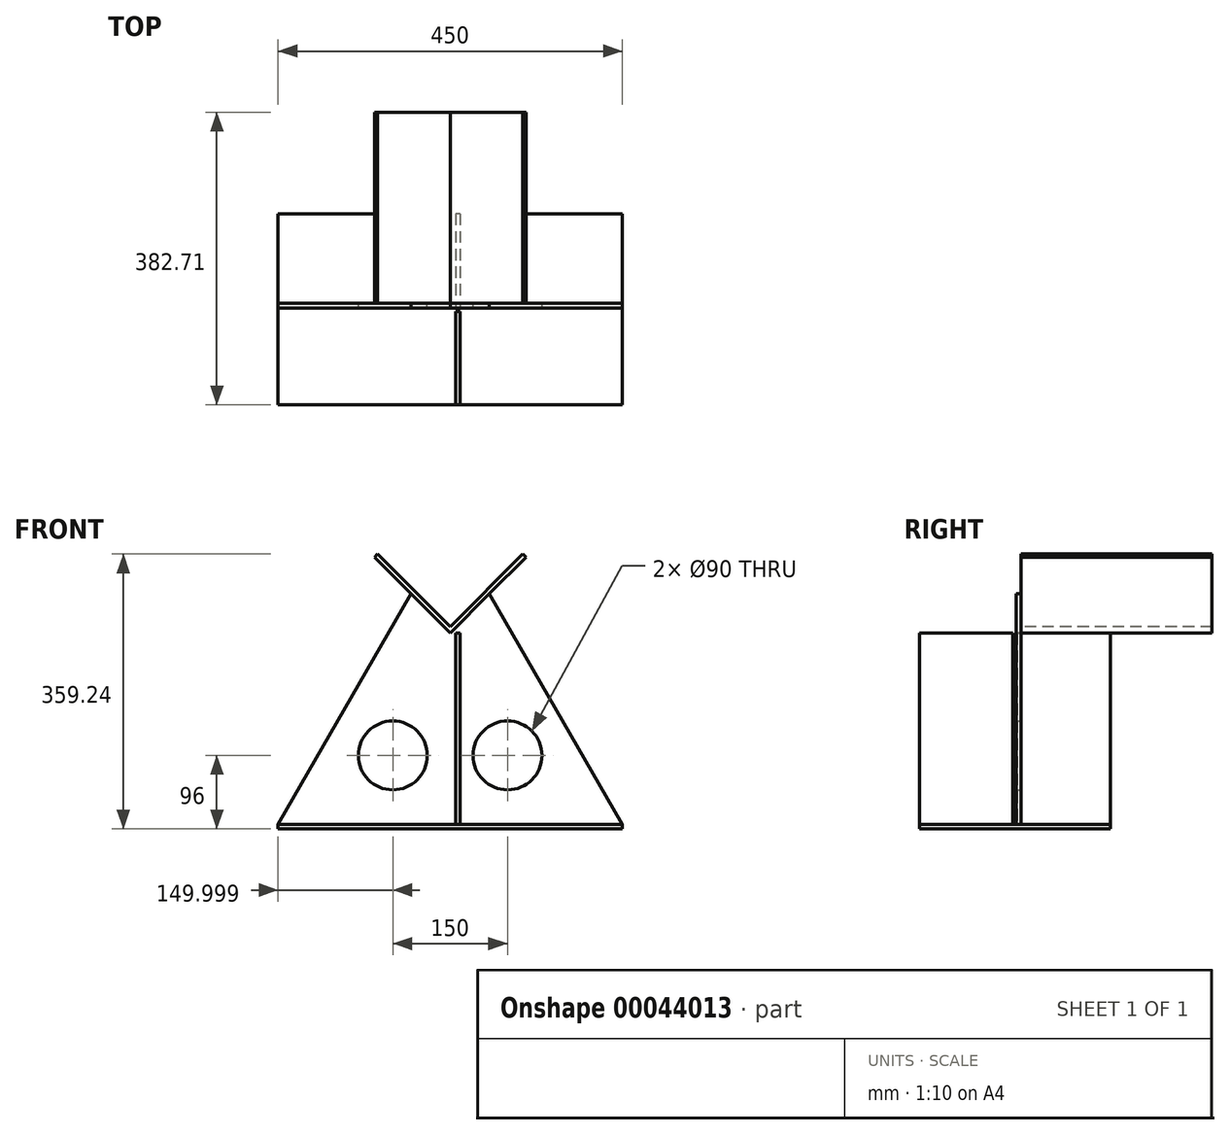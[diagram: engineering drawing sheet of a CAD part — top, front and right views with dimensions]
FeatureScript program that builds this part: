
annotation { "Feature Type Name" : "Feature", "Feature Type Description" : "" }
export const myFeature = defineFeature(function(context is Context, id is Id, definition is map)
    precondition{}
    {
        {
            var Q0;
            Q0=qCreatedBy(makeId("Top.planeOp"),FACE);
            var sketch = newSketch(context, id + "F0", { "sketchPlane" : qUnion([Q0])});
            skLineSegment(sketch, "E0.bottom", {"start": v(-231.25, -129.7) * mm, "end": v(218.75, -129.7) * mm});
            skLineSegment(sketch, "E0.top", {"start": v(-231.25, 120.3) * mm, "end": v(218.75, 120.3) * mm});
            skLineSegment(sketch, "E0.left", {"start": v(-231.25, -129.7) * mm, "end": v(-231.25, 120.3) * mm});
            skLineSegment(sketch, "E0.right", {"start": v(218.75, -129.7) * mm, "end": v(218.75, 120.3) * mm});
            skSolve(sketch);
        }
        {
            var Q0;
            Q0=qSketchRegion(id+"F0",true);
            var Q1;
            Q1=makeQuery(id+"F0.imprint","IMPRINT",FACE,{"disambiguationData":[TD([[makeQuery(id+"F0.imprint","IMPRINT",EDGE,{"derivedFrom":sQuery(id+"F0.wireOp",EDGE,"E0.bottom")}),1.0]])]});
            extrude(context, id + "F1", {"entities" : qUnion([Q0, Q1]), "depth" : 6 * mm});
        }
        {
            var Q0;
            Q0=qCreatedBy(makeId("Front.planeOp"),FACE);
            var sketch = newSketch(context, id + "F2", { "sketchPlane" : qUnion([Q0])});
            skLineSegment(sketch, "E1", {"start": v(-231.25, 6) * mm, "end": v(-57.39, 307.14) * mm});
            skLineSegment(sketch, "E2", {"start": v(218.75, 6) * mm, "end": v(44.89, 307.14) * mm});
            skLineSegment(sketch, "E3", {"start": v(-6.25, 256) * mm, "end": v(-57.39, 307.14) * mm});
            skLineSegment(sketch, "E4", {"start": v(-6.25, 256) * mm, "end": v(44.89, 307.14) * mm});
            skPoint(sketch, "E5.0", {"position": v(0, 0) * mm});
            skLineSegment(sketch, "E6", {"start": v(218.75, 6) * mm, "end": v(-231.25, 6) * mm});
            skCircle(sketch, "E7", {"center": v(-81.25, 96) * mm, "radius": 45 * mm});
            skCircle(sketch, "E8", {"center": v(68.75, 96) * mm, "radius": 45 * mm});
            skSolve(sketch);
        }
        {
            var Q0;
            Q0=makeQuery(id+"F2.imprint","IMPRINT",FACE,{"disambiguationData":[TD([[makeQuery(id+"F2.imprint","IMPRINT",EDGE,{"derivedFrom":sQuery(id+"F2.wireOp",EDGE,"E1")}),-1.0]])]});
            extrude(context, id + "F3", {"entities" : qUnion([Q0]), "depth" : 3 * mm, "hasSecondDirection" : true, "secondDirectionOppositeDirection" : true, "secondDirectionDepth" : 3 * mm});
        }
        {
            var Q0;
            Q0=makeQuery(id+"F1.opExtrude","CAP_FACE",FACE,{"disambiguationData":[OSD([sQuery(id+"F0.wireOp",EDGE,"E0.bottom"),sQuery(id+"F0.wireOp",EDGE,"E0.top"),sQuery(id+"F0.wireOp",EDGE,"E0.left"),sQuery(id+"F0.wireOp",EDGE,"E0.right")])],"isStart":false});
            var sketch = newSketch(context, id + "F4", { "sketchPlane" : qUnion([Q0])});
            skLineSegment(sketch, "E9", {"start": v(6.68, -7.7) * mm, "end": v(0.68, -7.7) * mm});
            skLineSegment(sketch, "E10", {"start": v(0.68, -7.7) * mm, "end": v(0.68, -129.7) * mm});
            skLineSegment(sketch, "E11", {"start": v(6.68, -7.7) * mm, "end": v(6.68, -129.7) * mm});
            skLineSegment(sketch, "E12", {"start": v(0.68, -129.7) * mm, "end": v(6.68, -129.7) * mm});
            skSolve(sketch);
        }
        {
            var Q0;
            Q0 = qSketchRegion(id + "F4", true);
            extrude(context, id + "F5", {"entities" : qUnion([Q0]), "depth" : 250 * mm});
        }
        {
            var Q0;
            Q0=makeQuery(id+"F5.opExtrude","SWEPT_BODY",BODY,{"disambiguationData":[OSD([sQuery(id+"F4.wireOp",EDGE,"E9"),sQuery(id+"F4.wireOp",EDGE,"E10"),sQuery(id+"F4.wireOp",EDGE,"E11"),sQuery(id+"F4.wireOp",EDGE,"E12")])]});
            transform(context, id + "F6", {"entities" : qUnion([Q0]), "transformType" : TransformType.TRANSLATION_3D, "dx" : 0 * mm, "dy" : 128 * mm, "dz" : 0 * mm, "makeCopy" : true});
        }
        {
            var Q0;
            Q0=makeQuery(id+"F3.opExtrude","CAP_FACE",FACE,{"disambiguationData":[OSD([sQuery(id+"F2.wireOp",EDGE,"E1"),sQuery(id+"F2.wireOp",EDGE,"E2"),sQuery(id+"F2.wireOp",EDGE,"E3"),sQuery(id+"F2.wireOp",EDGE,"E4"),sQuery(id+"F2.wireOp",EDGE,"E6")])],"isStart":true});
            var sketch = newSketch(context, id + "F7", { "sketchPlane" : qUnion([Q0])});
            skLineSegment(sketch, "E13", {"start": v(6.25, 256) * mm, "end": v(105.25, 355) * mm});
            skLineSegment(sketch, "E14", {"start": v(105.25, 355) * mm, "end": v(101, 359.24) * mm});
            skLineSegment(sketch, "E15", {"start": v(101, 359.24) * mm, "end": v(6.25, 264.49) * mm});
            skLineSegment(sketch, "E16", {"start": v(6.25, 264.49) * mm, "end": v(-88.5, 359.24) * mm});
            skLineSegment(sketch, "E17", {"start": v(-88.5, 359.24) * mm, "end": v(-92.74, 355) * mm});
            skLineSegment(sketch, "E18", {"start": v(-92.74, 355) * mm, "end": v(6.25, 256) * mm});
            skSolve(sketch);
        }
        {
            var Q0;
            Q0 = qSketchRegion(id + "F7", true);
            extrude(context, id + "F8", {"entities" : qUnion([Q0]), "depth" : 250 * mm});
        }
    });
